# Revit family: QF_BPRO_CCE-A mit Tablettführung_574929
name_source: partatom
category: Sonderausstattung
revit_build: Autodesk Revit 2018 (Build: 20190510_1515(x64)
units: mm (PartAtom-declared; Revit-internal decimal feet)

## family parameters
Arbeitsebenenbasiert = Nein
Beim Laden mit Abzugskörper schneiden = Nein
Bemaßung runder Anschluss = Durchmesser verwenden
Gemeinsam genutzt = Nein
Immer vertikal = Ja
Raumberechnungspunkt = Ja
Teiletyp = Normal

## types (1)
- CCE-A mit Tablettführung
    Artikel Nummer = 574929
    Beschreibung = Tablettspender, offene Ausführung;
mit seitlichen Tablettführungen;
max. 530 x 370 mm;
ca. 100 Tabletts;
    Beschreibung durch Hersteller analog Leistungsverzeichniskurztext = Abmessungen

Länge:					810 mm
Breite:					555 mm
Höhe:					900 mm


Ausführung

Aufbau
Der Tablettspender besteht komplett aus CNS 18/10. Die Oberfläche ist mikroliert. 
Der Tablettspender ist offen ausgeführt. Die Tabletts werden auf eine Plattform aufgesetzt. Diese ist allseitig aufgekantet (nicht an den Ecken bzgl. Reinigung), um das Verrutschen der Tabletts zu vermeiden.
Durch Ein- bzw. Aushängen der Zugfedern kann die Federspannung entsprechend dem Stapelgut reguliert werden, um eine gleichbleibende Ausgabehöhe zu gewährleisten.
Der Tablettspender ist speziell für den Einsatz am Band konzipiert.
Bedienseitig ist ein CNS- Schiebegriff angebracht.
Fahrbar ist der Spender mittels rostfreien Kunststoffrollen (4 Lenkrollen, 2 davon mit Feststeller mit 125 mm ø). Massive Stoßecken aus Kunststoff (Polyamid) an allen vier Ecken schützen vor Beschädigung.


Zubehör/ Optionen

•	Dekorausführung
•	weitere Zubehöre und Rollenausführungen siehe Gesamt-Preisliste



Technische Daten

Werkstoff:		CNS 18/10
Gewicht:		35 kg
Kapazität:		ca. 100 Tabletts,
		530 x 370 mm
Stapelhöhe:		700 mm
Max. Zuladung:		200 Kg

Besonderheit

•	Veränderung der Federspannung möglich
•	Ausführung für Einsatz am Band
•	zwei seitliche Tablettführungen
•	gemäß DIN 18665, Teil 6


Fabrikat

Hersteller:			B.PRO
Modell:				CCE-A
Best.Nr.:				574 929
    Beschreibung durch Hersteller analog Leistungsverzeichnislangtext = Abmessungen

Länge:					810 mm
Breite:					555 mm
Höhe:					900 mm


Ausführung

Aufbau
Der Tablettspender besteht komplett aus CNS 18/10. Die Oberfläche ist mikroliert. 
Der Tablettspender ist offen ausgeführt. Die Tabletts werden auf eine Plattform aufgesetzt. Diese ist allseitig aufgekantet (nicht an den Ecken bzgl. Reinigung), um das Verrutschen der Tabletts zu vermeiden.
Durch Ein- bzw. Aushängen der Zugfedern kann die Federspannung entsprechend dem Stapelgut reguliert werden, um eine gleichbleibende Ausgabehöhe zu gewährleisten.
Der Tablettspender ist speziell für den Einsatz am Band konzipiert.
Bedienseitig ist ein CNS- Schiebegriff angebracht.
Fahrbar ist der Spender mittels rostfreien Kunststoffrollen (4 Lenkrollen, 2 davon mit Feststeller mit 125 mm ø). Massive Stoßecken aus Kunststoff (Polyamid) an allen vier Ecken schützen vor Beschädigung.


Zubehör/ Optionen

•	Dekorausführung
•	weitere Zubehöre und Rollenausführungen siehe Gesamt-Preisliste



Technische Daten

Werkstoff:		CNS 18/10
Gewicht:		35 kg
Kapazität:		ca. 100 Tabletts,
		530 x 370 mm
Stapelhöhe:		700 mm
Max. Zuladung:		200 Kg

Besonderheit

•	Veränderung der Federspannung möglich
•	Ausführung für Einsatz am Band
•	zwei seitliche Tablettführungen
•	gemäß DIN 18665, Teil 6


Fabrikat

Hersteller:			B.PRO
Modell:				CCE-A
Best.Nr.:				574 929
    Gerätegewicht Netto = 35.00 kg
    Großküchengerätezuordnung = Ja
    Hersteller = B.PRO GmbH
    Höhe = 900 mm  [stored 2.95276 ft]
    Internetadresse Gerätehersteller = https://www.bpro-solutions.com
    Internetadresse für Ersatzteilliste = https://www.bpro-solutions.com
    Kosten = 1527.6 $
    Länge Gerätebreite = 810 mm
    Länge Tablettträger = 540 mm  [stored 1.77165 ft]
    Länge Tragarm = 509 mm
    Material = QF_Metal-Stainless-Steel_general
    Material_Stoßschutz = QF_Rubber-Black-Matt
    Modell = CCE-A
    Sockelhöhe = 160 mm  [stored 0.524934 ft]
    Tablettführungen = Ja
    Tablettträger OK = 575 mm
    Tiefe = 555 mm  [stored 1.82087 ft]
    Tiefe Tablettträger = 380 mm
    Typenkommentare = Tablettspender, offen mit Tablettführungen
    URL = https://www.bpro-solutions.com
    Warnhinweise = Ausführliche Gefahrenhinweise entnehmen Sie der Betriebsanleitung.
    Zubehör = Nein

note: [stored X ft] marks values corroborated as IEEE doubles in the binary element streams (Revit-internal decimal feet)
